# Revit family: Floor_Drain-Josam-30000-A
name_source: partatom
category: Plumbing Fixtures
revit_build: Autodesk Revit MEP 2012 (Build: 20110309_2315(x64)
units: mm (PartAtom-declared; Revit-internal decimal feet)

## types (3) — shared parameters
04 CSI = 22 40 00
B = 0' - 5"
B Radius = 0' - 2 1/2"
Default Elevation = 4' - 0"
Description = Floor drain - cast iron
Inner Cleanout body = Metal - Josam - Brass - Satin
Manufacturer = Josam Company
Manufacturer Fax = 800-627-0008
Model = 30000-A
Outer Cleanout Body = Metal - Josam - Anodized- Dark Green Satin
Product Line = Josam
Product Page URL = http://www.josam.com
Product Type = Round Top
Subcategory = Floor Drain
Top Cleanout = Metal - Josam - Plate - Mesh
URL = http://www.josam.com
X = 0' - 0 3/4"

## per-type parameters (varying)
| type | Pipe Size Diameter | Pipe Size Radius |
| 2In Diameter | 0' - 2" | 0' - 1" |
| 3In Diameter | 0' - 3" | 0' - 1 1/2" |
| 4In Diameter | 0' - 4" | 0' - 2" |

## geometry (parser evidence)
native form markers: Blend x5, Sweep x7
no freeform markers — native parametric forms only
